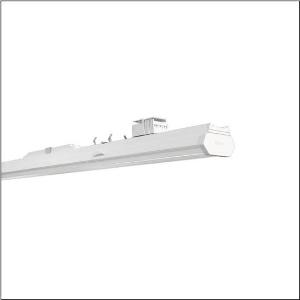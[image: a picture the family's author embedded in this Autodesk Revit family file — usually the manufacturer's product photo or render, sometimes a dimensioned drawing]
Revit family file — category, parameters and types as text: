
# Revit family: licross_r__21_protected_ho_52td11dn4dxs_f76a
name_source: partatom
category: Lighting Fixtures
units: mm (PartAtom-declared; Revit-internal decimal feet)

## family parameters
Cut with Voids When Loaded = No
Host = Face
Light Source = No
Part Type = Normal
Room Calculation Point = No
Round Connector Dimension = Use Diameter
Shared = No

## types (1)
- --- (1 x LED, 13000 lm, 73.1 W, 4000K)
    Apparent Load = 73 VA
    CIE Flux Codes = 84 94 98 99 100
    Color Rendering = 80
    Color Temperature = 4000K
    Default Elevation = 1800 mm
    Description = Licross® 21 Protected HO, luminaire insert, of sheet steel, galvanised, coil coated, white, length: 1.500mm, width: 90mm, height: 103mm, LED rated luminous flux: 13.000lm, light colour: 840, control gear: DALI 2, with plug, 5-pole, with phase selection, mains connection: 220..240V, AC, 50/60Hz, rated input power: 73W, halogen-free wiring, primary light control with lens, of plastic, primary optical cover: cover, of PMMA, light emission: direct distribution, primary light characteristic: symmetric, protection rating (complete): IP54, insulation class (complete): insulation class I (protective earthing), certification: CE, ENEC, VDE, UKCA, protection symbol: D if used in an environment with non-conductive dust loads with corresponding accessories, impact resistance: IK06, permissible ambient temperature for indoor applications: -25..+40°C, corresponds to IFS (International Featured Standards) requirements for safety and quality in the food industry, reducing of maximum allowable ambient temperature of 5°C with ceiling mounting, LABS conformity tested according to VDMA 24364:2018-05, packaging unit: 1 piece
    Height = 92 mm
    Lamp = 1 x LED
    Lamp Light Flux = 13000 lm
    Lamp Power = 73.1 W
    Lamp count = 1
    Length = 1500 mm
    Luminous efficacy = 178 lm/W
    Manufacturer = Siteco
    ModVariant = No
    Model = 52TD11DN4DXS
    Mounting Place = Ceiling
    Mounting Type = Pendant
    Number of Poles = 1
    OnlyDefault = Yes
    Power Factor = 1
    Product Name = Licross® 21 Protected HO
    Product group = luminaire insert
    ProductGroupID = 901
    Protection Class = Protection class I
    Protection Degree = IP 54
    RLX_Detail_Level = 1
    RLX_Emergency_Light_Flux = 0 lm
    RLX_Emergency_Type = 0
    RLX_Emergency_Type_DB = No
    RlxData = <blob elided: 24269 chars, md5=31be8be0>
    Socket = socket
    Standby Power = 0 W
    System Light Flux = 13000 lm
    System Power = 73 W
    Type Comments = factory setting: luminous flux: 100 % | dim-lin: 254 | 417 mA
    Type Image = l_1256148.jpg
    URL = http://relux.com
    VarID = @adj_060077
    Voltage = 0 V
    Weight = 0.00 kg
    Width = 88 mm

## geometry (parser evidence)
native form markers: Blend x4, Sweep x13
no freeform markers — native parametric forms only
